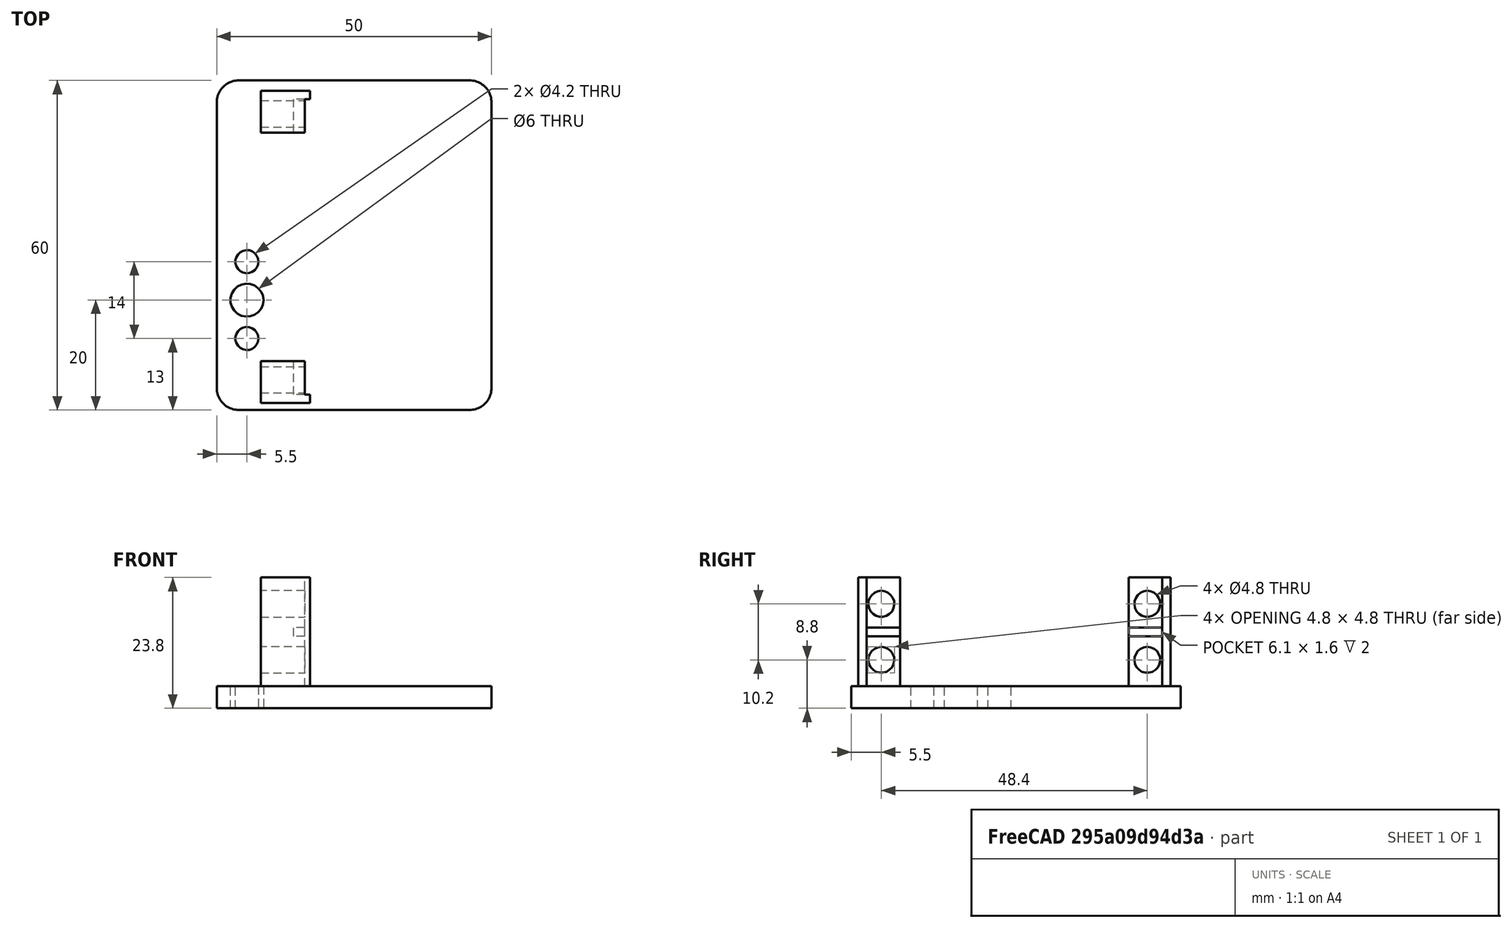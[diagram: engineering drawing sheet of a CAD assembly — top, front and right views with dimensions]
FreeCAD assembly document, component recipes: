
FREECAD ASSEMBLY — COMPONENT RECIPES ("Top_Base")

This assembly document has 2 components, labeled P0..P1 below (a component is one placed body or linked part). 2 of them carry a construction recipe — the FreeCAD feature program that regenerates the part from scratch, quoted from this document or its linked companion documents; the rest are supplied as boundary geometry only. No exploded tour is included for this assembly.
COMPONENT P0 — recipe-attached ("Link(Servo_Horn)", modeled in this document).
Construction recipe (the document's own serialized feature program — sketch geometry with constraints, then the solid features built on it; lengths are millimeters unless a unit is written):

FEATURE [PartDesign::SubShapeBinder] Binder  label="Binder(Pocket)"
  BindCopyOnChange = 0
  BindMode = 0
  ClaimChildren = false
  Context = -> Assembly [Parts.Part.Binder.]
  EdgeTolerance = 1e-06
  FillStyle = 0
  Fuse = false
  InvalidShape = false
  MakeFace = true
  MergeEdges = true
  OffsetFill = false
  OffsetIntersection = false
  OffsetJoinType = 0
  OffsetOpenResult = false
  Outline = false
  PartialLoad = false
  Relative = true
  SplitEdges = false
  Support = -> [Link[Body.Pocket.Face9]]
  TightBound = false
  TreeRank = 30
  ValidateShape = false
  _Version = 8
FEATURE [Sketcher::SketchObject] Sketch
  ArcFitTolerance = 1e-06
  AttachmentSupport = -> [Binder]
  ExternalBSplineMaxDegree = 5
  ExternalBSplineTolerance = 0.0001
  ExternalGeometry = -> [Binder]
  FullyConstrained = true
  InternalTolerance = 1e-06
  InvalidShape = false
  MakeInternals = false
  MapMode = 5
  Placement = pos=(0,0,0) rot=(0,1.01411,0;0rad)
  Support = -> [Binder]
  TreeRank = 31
  ValidateShape = false
  sketch-geometry (6):
    g0: GeomPoint [constr] X=0 Y=0 Z=0
    g1: LineSegment StartX=-5.5 StartY=40 StartZ=0 EndX=44.5 EndY=40 EndZ=0
    g2: LineSegment StartX=44.5 StartY=40 StartZ=0 EndX=44.5 EndY=-20 EndZ=0
    g3: LineSegment StartX=44.5 StartY=-20 StartZ=0 EndX=-5.5 EndY=-20 EndZ=0
    g4: LineSegment StartX=-5.5 StartY=-20 StartZ=0 EndX=-5.5 EndY=40 EndZ=0
    g5: GeomPoint [constr] X=-5.5 Y=0 Z=0
  constraints (15):
    c: Coincident(g0,g-1)
    c: Coincident(g1,g2)
    c: Coincident(g2,g3)
    c: Coincident(g3,g4)
    c: Coincident(g4,g1)
    c: Horizontal(g1)
    c: Horizontal(g3)
    c: Vertical(g2)
    c: Distance(g1) = 50
    c: PointOnObject(g5,g-3)
    c: PointOnObject(g5,g-1)
    c: Vertical(g4)
    c: DistanceY(g3,g0) = 20
    c: DistanceY(g0,g1) = 40
    c: PointOnObject(g5,g4)
FEATURE [PartDesign::Pad] Pad
  AddSubType = 0
  AlongSketchNormal = false
  AutoTaperInnerAngle = true
  CheckUpToFaceLimits = true
  ClaimChildren = false
  Direction = (8.74228e-08,-2.3e-15,1)
  Fit = 0
  FitJoin = 0
  InnerFit = 0
  InnerFitJoin = 0
  InvalidShape = false
  Length = 4
  Length2 = 10
  Linearize = true
  NewSolid = false
  Profile = -> Sketch
  ReferenceAxis = -> Sketch [N_Axis]
  Refine = true
  Suppress = false
  TaperInnerAngle = 0
  TaperInnerAngleRev = 0
  TreeRank = 32
  Type = 0
  ValidateShape = true
  _ProfileBasedVersion = 1
FEATURE [PartDesign::Fillet] Fillet
  AddSubType = 0
  Base = -> Pad [Edge8,Edge5,Edge2,Edge1]
  BaseFeature = -> Pad
  InvalidShape = false
  NewSolid = false
  Radius = 4
  Refine = true
  SupportTransform = false
  Suppress = false
  TreeRank = 33
  UseAllEdges = false
  ValidateShape = true
FEATURE [Part::SubShapeBinder] Import  label="Import(Pocket)"
  BindCopyOnChange = 0
  BindMode = 0
  ClaimChildren = false
  Context = -> Assembly [Parts.Part.Body.Import.]
  EdgeTolerance = 1e-06
  FillStyle = 0
  Fuse = false
  InvalidShape = false
  MakeFace = false
  MergeEdges = true
  OffsetFill = false
  OffsetIntersection = false
  OffsetJoinType = 0
  OffsetOpenResult = false
  Outline = false
  PartialLoad = false
  Relative = true
  SplitEdges = false
  Support = -> [Link[Body.Pocket.]]
  TightBound = false
  TreeRank = 36
  ValidateShape = false
  _Version = 8
FEATURE [Sketcher::SketchObject] Sketch001
  ArcFitTolerance = 1e-06
  AttachmentSupport = -> [Fillet]
  ExternalBSplineMaxDegree = 5
  ExternalBSplineTolerance = 0.0001
  ExternalGeometry = -> [Binder,Import]
  FullyConstrained = true
  InternalTolerance = 1e-06
  InvalidShape = false
  MakeInternals = false
  MapMode = 5
  Placement = pos=(3.49691e-07,-9e-15,4) rot=(0,1.01411,0;0rad)
  Support = -> [Fillet]
  TreeRank = 34
  ValidateShape = false
  sketch-geometry (2):
    g0: Circle CenterX=-1.18011e-06 CenterY=7 CenterZ=0 NormalX=0 NormalY=0 NormalZ=1 AngleXU=0 Radius=2.1
    g1: Circle CenterX=1.18011e-06 CenterY=-7 CenterZ=0 NormalX=0 NormalY=0 NormalZ=1 AngleXU=0 Radius=2.1
  constraints (4):
    c: Coincident(g0,g-4)
    c: Coincident(g1,g-3)
    c: Equal(g1,g0)
    c: Diameter(g0) = 4.2
FEATURE [PartDesign::Pocket] Pocket
  AddSubType = 1
  AlongSketchNormal = false
  AutoTaperInnerAngle = true
  BaseFeature = -> Fillet
  CheckUpToFaceLimits = true
  ClaimChildren = false
  Direction = (-8.74228e-08,2.3e-15,-1)
  Fit = 0
  FitJoin = 0
  InnerFit = 0
  InnerFitJoin = 0
  InvalidShape = false
  Length = 5
  Length2 = 10
  Linearize = true
  NewSolid = false
  Profile = -> Sketch001
  ReferenceAxis = -> Sketch001 [N_Axis]
  Refine = true
  Suppress = false
  TaperInnerAngle = 0
  TaperInnerAngleRev = 0
  TreeRank = 35
  Type = 1
  ValidateShape = true
  _ProfileBasedVersion = 1
  _Version = 1
FEATURE [PartDesign::SubShapeBinder] Binder001  label="Binder001(*Hitec_D625MW)"
  BindCopyOnChange = 0
  BindMode = 0
  ClaimChildren = false
  Context = -> Assembly [Parts.Part.Body.Binder001.]
  EdgeTolerance = 1e-06
  FillStyle = 0
  Fuse = false
  InvalidShape = false
  MakeFace = true
  MergeEdges = true
  OffsetFill = false
  OffsetIntersection = false
  OffsetJoinType = 0
  OffsetOpenResult = false
  Outline = false
  PartialLoad = false
  Relative = true
  SplitEdges = false
  Support = -> [Link001]
  TightBound = false
  TreeRank = 61
  ValidateShape = false
  _Version = 8
FEATURE [Sketcher::SketchObject] Sketch002
  ArcFitTolerance = 1e-06
  AttachmentSupport = -> [Pocket]
  ExternalBSplineMaxDegree = 5
  ExternalBSplineTolerance = 0.0001
  ExternalGeometry = -> [Binder001]
  FullyConstrained = true
  InternalTolerance = 1e-06
  InvalidShape = false
  MakeInternals = false
  MapMode = 5
  Placement = pos=(3.49691e-07,-9e-15,4) rot=(0,1.01411,0;0rad)
  Support = -> [Pocket]
  TreeRank = 62
  ValidateShape = false
  sketch-geometry (12):
    g0: LineSegment StartX=2.5 StartY=-11.1 StartZ=0 EndX=10.5 EndY=-11.1 EndZ=0
    g1: LineSegment StartX=11.5 StartY=-18.7 StartZ=0 EndX=2.5 EndY=-18.7 EndZ=0
    g2: LineSegment StartX=2.5 StartY=-18.7 StartZ=0 EndX=2.5 EndY=-11.1 EndZ=0
    g3: LineSegment StartX=2.50001 StartY=38.1 StartZ=0 EndX=11.5 EndY=38.1 EndZ=0
    g4: LineSegment StartX=10.5 StartY=30.5 StartZ=0 EndX=2.50001 EndY=30.5 EndZ=0
    g5: LineSegment StartX=2.50001 StartY=30.5 StartZ=0 EndX=2.50001 EndY=38.1 EndZ=0
    g6: LineSegment StartX=10.5 StartY=-11.1 StartZ=0 EndX=10.5 EndY=-17.2 EndZ=0
    g7: LineSegment StartX=10.5 StartY=-17.2 StartZ=0 EndX=11.5 EndY=-17.2 EndZ=0
    g8: LineSegment StartX=11.5 StartY=-17.2 StartZ=0 EndX=11.5 EndY=-18.7 EndZ=0
    g9: LineSegment StartX=10.5 StartY=36.6 StartZ=0 EndX=10.5 EndY=30.5 EndZ=0
    g10: LineSegment StartX=10.5 StartY=36.6 StartZ=0 EndX=11.5 EndY=36.6 EndZ=0
    g11: LineSegment StartX=11.5 StartY=36.6 StartZ=0 EndX=11.5 EndY=38.1 EndZ=0
  constraints (36):
    c: Coincident(g0,g6)
    c: Coincident(g1,g2)
    c: Coincident(g2,g0)
    c: Horizontal(g0)
    c: Horizontal(g1)
    c: Vertical(g2)
    c: Coincident(g9,g4)
    c: Coincident(g4,g5)
    c: Coincident(g5,g3)
    c: Horizontal(g3)
    c: Horizontal(g4)
    c: Vertical(g5)
    c: Equal(g2,g5)
    c: Equal(g3,g1)
    c: Distance(g-7,g0) = 0.5
    c: Distance(g-8,g4) = 0.5
    c: Vertical(g6)
    c: PointOnObject(g-3,g6)
    c: Coincident(g7,g6)
    c: Horizontal(g7)
    c: Coincident(g8,g7)
    c: Vertical(g8)
    c: Coincident(g1,g8)
    c: Distance(g6,g-4) = 0.1
    c: Distance(g7) = 1
    c: Vertical(g9)
    c: Coincident(g10,g9)
    c: Horizontal(g10)
    c: Coincident(g11,g10)
    c: Vertical(g11)
    c: Coincident(g3,g11)
    c: Equal(g10,g7)
    c: PointOnObject(g-5,g9)
    c: Equal(g6,g9)
    c: Distance(g8) = 1.5
    c: Distance(g0) = 8
FEATURE [PartDesign::Pad] Pad001
  AddSubType = 0
  AlongSketchNormal = false
  AutoTaperInnerAngle = true
  BaseFeature = -> Pocket
  CheckUpToFaceLimits = true
  ClaimChildren = false
  Direction = (8.74228e-08,-2.3e-15,1)
  Fit = 0
  FitJoin = 0
  InnerFit = 0
  InnerFitJoin = 0
  InvalidShape = false
  Length = 10
  Length2 = 10
  Linearize = true
  NewSolid = false
  Profile = -> Sketch002
  ReferenceAxis = -> Sketch002 [N_Axis]
  Refine = true
  Suppress = false
  TaperInnerAngle = 0
  TaperInnerAngleRev = 0
  TreeRank = 63
  Type = 3
  UpToFace = -> Binder001 [Face10]
  ValidateShape = true
  _ProfileBasedVersion = 1
FEATURE [PartDesign::Plane] DatumPlane
  AttachmentSupport = -> [Pad001]
  InvalidShape = false
  Length = 13.9
  MapMode = 45
  MinimumLength = 10
  MinimumWidth = 10
  Placement = pos=(10.5,9.7,13.9) rot=(0.707107,0,0.707107;3.14159rad)
  ResizeMode = 0
  Support = -> [Pad001]
  TreeRank = 64
  ValidateShape = false
  Width = 18.8
FEATURE [Sketcher::SketchObject] Sketch003
  ArcFitTolerance = 1e-06
  AttachmentSupport = -> [DatumPlane]
  ExternalBSplineMaxDegree = 5
  ExternalBSplineTolerance = 0.0001
  ExternalGeometry = -> [Binder001]
  FullyConstrained = true
  InternalTolerance = 1e-06
  InvalidShape = false
  MakeInternals = false
  MapMode = 5
  Placement = pos=(10.5,9.7,13.9) rot=(0.707107,0,0.707107;3.14159rad)
  Support = -> [DatumPlane]
  TreeRank = 65
  ValidateShape = false
  sketch-geometry (4):
    g0: Circle CenterX=5.1 CenterY=24.2 CenterZ=0 NormalX=0 NormalY=0 NormalZ=1 AngleXU=0 Radius=2.4
    g1: Circle CenterX=-5.1 CenterY=24.2 CenterZ=0 NormalX=0 NormalY=0 NormalZ=1 AngleXU=0 Radius=2.4
    g2: Circle CenterX=5.1 CenterY=-24.2 CenterZ=0 NormalX=0 NormalY=0 NormalZ=1 AngleXU=0 Radius=2.4
    g3: Circle CenterX=-5.1 CenterY=-24.2 CenterZ=0 NormalX=0 NormalY=0 NormalZ=1 AngleXU=0 Radius=2.4
  constraints (8):
    c: Coincident(g0,g-5)
    c: Coincident(g1,g-6)
    c: Coincident(g2,g-3)
    c: Coincident(g3,g-4)
    c: Equal(g3,g2)
    c: Equal(g2,g0)
    c: Equal(g0,g1)
    c: Diameter(g0) = 4.8
FEATURE [PartDesign::Pocket] Pocket001
  AddSubType = 1
  AlongSketchNormal = false
  AutoTaperInnerAngle = true
  BaseFeature = -> Pad001
  CheckUpToFaceLimits = true
  ClaimChildren = false
  Direction = (-1,1.76265e-07,8.74228e-08)
  Fit = 0
  FitJoin = 0
  InnerFit = 0
  InnerFitJoin = 0
  InvalidShape = false
  Length = 5
  Length2 = 10
  Linearize = true
  Midplane = true
  NewSolid = false
  Profile = -> Sketch003
  ReferenceAxis = -> Sketch003 [N_Axis]
  Refine = true
  Suppress = false
  TaperInnerAngle = 0
  TaperInnerAngleRev = 0
  TreeRank = 66
  Type = 1
  ValidateShape = true
  _ProfileBasedVersion = 1
  _Version = 1
FEATURE [Sketcher::SketchObject] Sketch004
  ArcFitTolerance = 1e-06
  AttachmentSupport = -> [DatumPlane]
  ExternalBSplineMaxDegree = 5
  ExternalBSplineTolerance = 0.0001
  ExternalGeometry = -> [Binder001,Pocket001]
  FullyConstrained = true
  InternalTolerance = 1e-06
  InvalidShape = false
  MakeInternals = false
  MapMode = 5
  Placement = pos=(10.5,9.7,13.9) rot=(0.707107,0,0.707107;3.14159rad)
  Support = -> [DatumPlane]
  TreeRank = 67
  ValidateShape = false
  sketch-geometry (8):
    g0: LineSegment StartX=0.8 StartY=26.9 StartZ=0 EndX=-0.8 EndY=26.9 EndZ=0
    g1: LineSegment StartX=-0.8 StartY=26.9 StartZ=0 EndX=-0.8 EndY=20.8 EndZ=0
    g2: LineSegment StartX=-0.8 StartY=20.8 StartZ=0 EndX=0.8 EndY=20.8 EndZ=0
    g3: LineSegment StartX=0.8 StartY=20.8 StartZ=0 EndX=0.8 EndY=26.9 EndZ=0
    g4: LineSegment StartX=0.8 StartY=-20.8 StartZ=0 EndX=-0.8 EndY=-20.8 EndZ=0
    g5: LineSegment StartX=-0.8 StartY=-20.8 StartZ=0 EndX=-0.8 EndY=-26.9 EndZ=0
    g6: LineSegment StartX=-0.8 StartY=-26.9 StartZ=0 EndX=0.8 EndY=-26.9 EndZ=0
    g7: LineSegment StartX=0.8 StartY=-26.9 StartZ=0 EndX=0.8 EndY=-20.8 EndZ=0
  constraints (22):
    c: Coincident(g0,g1)
    c: Coincident(g1,g2)
    c: Coincident(g2,g3)
    c: Coincident(g3,g0)
    c: Horizontal(g2)
    c: Vertical(g1)
    c: Vertical(g3)
    c: PointOnObject(g0,g-9)
    c: PointOnObject(g1,g-7)
    c: Symmetric(g0,g0,g-2)
    c: Distance(g-5,g3) = 0.2
    c: Coincident(g4,g5)
    c: Coincident(g5,g6)
    c: Coincident(g6,g7)
    c: Coincident(g7,g4)
    c: Horizontal(g4)
    c: Vertical(g5)
    c: Vertical(g7)
    c: PointOnObject(g4,g-8)
    c: PointOnObject(g5,g-10)
    c: Symmetric(g5,g6,g-2)
    c: Distance(g-3,g7) = 0.2
FEATURE [PartDesign::Pocket] Pocket002
  AddSubType = 1
  AlongSketchNormal = false
  AutoTaperInnerAngle = true
  BaseFeature = -> Pocket001
  CheckUpToFaceLimits = true
  ClaimChildren = false
  Direction = (-1,1.76265e-07,8.74228e-08)
  Fit = 0
  FitJoin = 0
  InnerFit = 0
  InnerFitJoin = 0
  InvalidShape = false
  Length = 4
  Length2 = 10
  Linearize = true
  Midplane = true
  NewSolid = false
  Profile = -> Sketch004
  ReferenceAxis = -> Sketch004 [N_Axis]
  Refine = true
  Suppress = false
  TaperInnerAngle = 0
  TaperInnerAngleRev = 0
  TreeRank = 68
  Type = 0
  ValidateShape = true
  _ProfileBasedVersion = 1
  _Version = 1
FEATURE [PartDesign::Body] Body
  AutoGroupSolids = false
  ClaimAllChildren = false
  ExportMode = 0
  Group = -> [Binder,Sketch,Pad,Fillet,Sketch001,Pocket,Import,Binder001,Sketch002,Pad001,DatumPlane,Sketch003,Pocket001,Sketch004,Pocket002]
  InvalidShape = false
  Origin = -> Origin001
  Tip = -> Pocket002
  TreeRank = 29
  ValidateShape = false
  _ExportChildren = -> [Binder,Pad,Fillet,Pocket,Import,Binder001,Pad001,DatumPlane,Pocket001,Pocket002]
  _GroupVersion = 1
COMPONENT P1 — same part as P0; its construction recipe is shown at P0.
PROVENANCE & LICENSES
A FreeCAD (.FCStd) document from a public repository crawl; recipes are the document's own serialized feature recipes (and, for linked parts, companion documents' recipes).
License: gpl-3.0.
